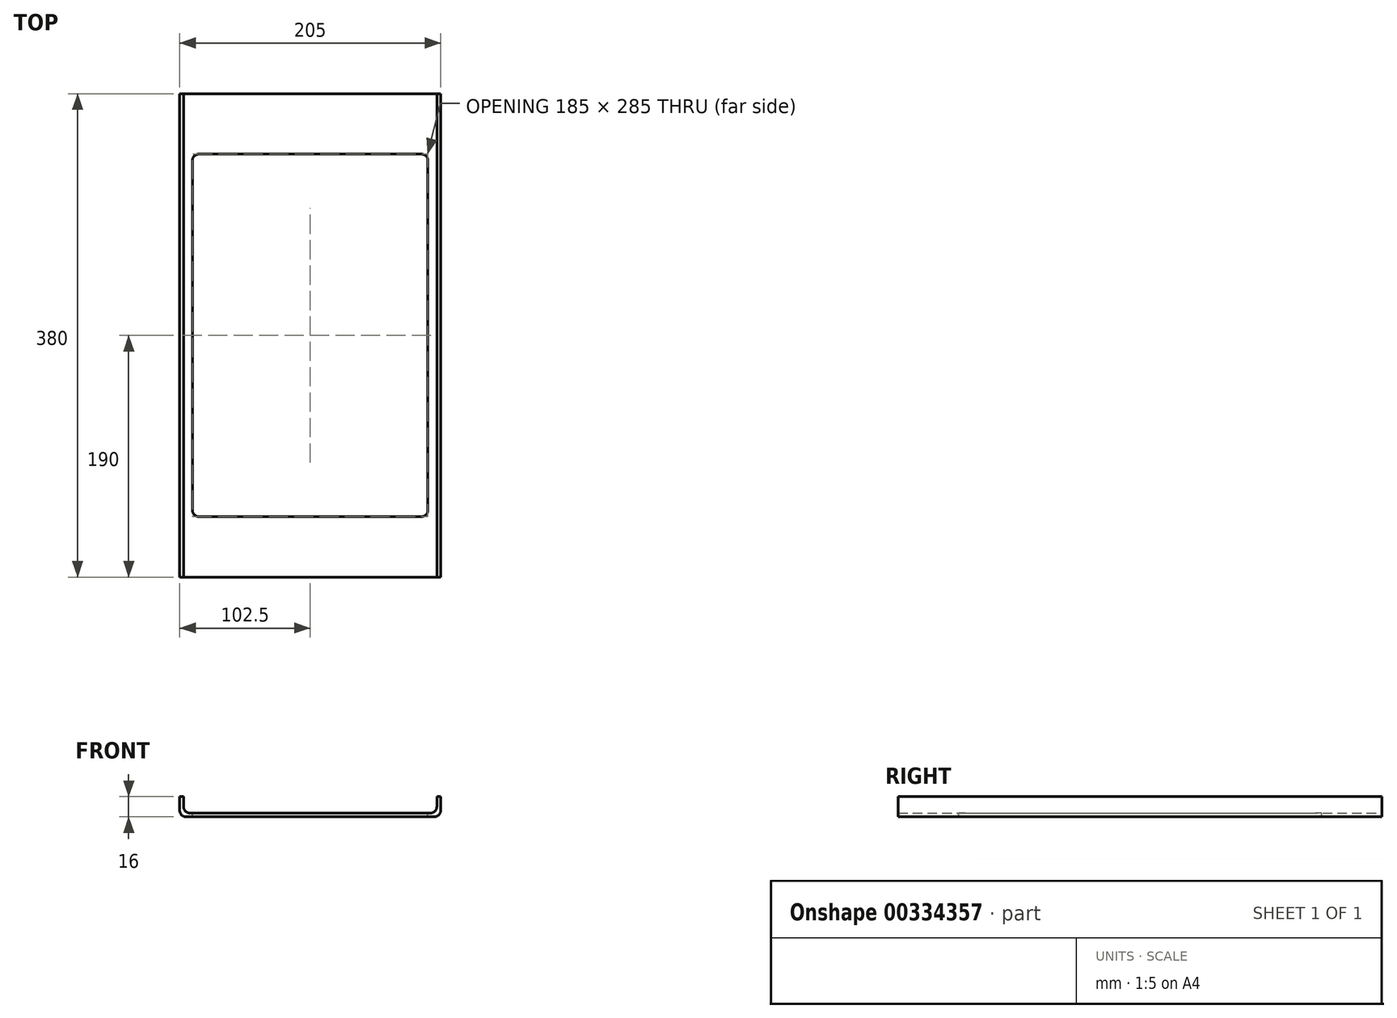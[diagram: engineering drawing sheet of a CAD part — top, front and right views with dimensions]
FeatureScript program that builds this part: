
annotation { "Feature Type Name" : "Feature", "Feature Type Description" : "" }
export const myFeature = defineFeature(function(context is Context, id is Id, definition is map)
    precondition{}
    {
        {
            var Q0;
            Q0=qCreatedBy(makeId("Front.planeOp"),FACE);
            var sketch = newSketch(context, id + "F0", { "sketchPlane" : qUnion([Q0])});
            skLineSegment(sketch, "E0.top", {"start": v(-102.5, -16) * mm, "end": v(102.5, -16) * mm});
            skLineSegment(sketch, "E0.left", {"start": v(-102.5, 0) * mm, "end": v(-102.5, -16) * mm});
            skLineSegment(sketch, "E0.right", {"start": v(102.5, 0) * mm, "end": v(102.5, -16) * mm});
            skPoint(sketch, "E0.middle", {"position": v(0, 0) * mm});
            skLineSegment(sketch, "E1.top", {"start": v(-99.5, -13) * mm, "end": v(99.5, -13) * mm});
            skLineSegment(sketch, "E1.left", {"start": v(-99.5, 0) * mm, "end": v(-99.5, -13) * mm});
            skLineSegment(sketch, "E1.right", {"start": v(99.5, 0) * mm, "end": v(99.5, -13) * mm});
            skLineSegment(sketch, "E2", {"start": v(102.5, 0) * mm, "end": v(99.5, 0) * mm});
            skPoint(sketch, "E0.bottom.end.orphan", {"position": v(102.5, 16) * mm});
            skPoint(sketch, "E1.bottom.end.orphan", {"position": v(99.5, 13) * mm});
            skLineSegment(sketch, "E3.trimOffspring", {"start": v(-99.5, 0) * mm, "end": v(-102.5, 0) * mm});
            skPoint(sketch, "E4.orphan", {"position": v(-102.5, 16) * mm});
            skPoint(sketch, "E5.orphan", {"position": v(-99.5, 13) * mm});
            skSolve(sketch);
        }
        {
            var Q0;
            Q0=qSketchRegion(id+"F0",true);
            extrude(context, id + "F1", {"entities" : qUnion([Q0]), "depth" : 380 * mm});
        }
        {
            var Q0;
            Q0=makeQuery(id+"F1.opExtrude","SWEPT_FACE",FACE,{"disambiguationData":[OSD([sQuery(id+"F0.wireOp",EDGE,"E1.top")])]});
            var sketch = newSketch(context, id + "F2", { "sketchPlane" : qUnion([Q0])});
            skLineSegment(sketch, "E6.bottom", {"start": v(-92.5, -332.5) * mm, "end": v(92.5, -332.5) * mm});
            skLineSegment(sketch, "E6.top", {"start": v(-92.5, -47.5) * mm, "end": v(92.5, -47.5) * mm});
            skLineSegment(sketch, "E6.left", {"start": v(-92.5, -332.5) * mm, "end": v(-92.5, -47.5) * mm});
            skLineSegment(sketch, "E6.right", {"start": v(92.5, -332.5) * mm, "end": v(92.5, -47.5) * mm});
            skPoint(sketch, "E6.middle", {"position": v(0, -190) * mm});
            skSolve(sketch);
        }
        {
            var Q0;
            Q0=makeQuery(id+"F2.imprint","IMPRINT",FACE,{"disambiguationData":[TD([[makeQuery(id+"F2.imprint","IMPRINT",EDGE,{"derivedFrom":sQuery(id+"F2.wireOp",EDGE,"E6.bottom")}),1.0]])]});
            extrude(context, id + "F3", {"entities" : qUnion([Q0]), "operationType" : NewBodyOperationType.REMOVE, "oppositeDirection" : true, "depth" : 3 * mm});
        }
        {
            var Q0;
            Q0=makeQuery(id+"F3.boolean.opBoolean","COPY",EDGE,{"derivedFrom":makeQuery(id+"F3.opExtrude","SWEPT_EDGE",EDGE,{"disambiguationData":[OSD([sQuery(id+"F2.wireOp",EDGE,"E6.top"),sQuery(id+"F2.wireOp",EDGE,"E6.left")])]})});
            var Q1;
            Q1=makeQuery(id+"F3.boolean.opBoolean","COPY",EDGE,{"derivedFrom":makeQuery(id+"F3.opExtrude","SWEPT_EDGE",EDGE,{"disambiguationData":[OSD([sQuery(id+"F2.wireOp",EDGE,"E6.top"),sQuery(id+"F2.wireOp",EDGE,"E6.right")])]})});
            var Q2;
            Q2=makeQuery(id+"F3.boolean.opBoolean","COPY",EDGE,{"derivedFrom":makeQuery(id+"F3.opExtrude","SWEPT_EDGE",EDGE,{"disambiguationData":[OSD([sQuery(id+"F2.wireOp",EDGE,"E6.bottom"),sQuery(id+"F2.wireOp",EDGE,"E6.left")])]})});
            var Q3;
            Q3=makeQuery(id+"F3.boolean.opBoolean","COPY",EDGE,{"derivedFrom":makeQuery(id+"F3.opExtrude","SWEPT_EDGE",EDGE,{"disambiguationData":[OSD([sQuery(id+"F2.wireOp",EDGE,"E6.bottom"),sQuery(id+"F2.wireOp",EDGE,"E6.right")])]})});
            fillet(context, id + "F4", {"entities" : qUnion([Q0, Q1, Q2, Q3]), "radius" : 5 * mm, "tangentPropagation" : true, "allowEdgeOverflow" : false});
        }
        {
            var Q0;
            Q0=makeQuery(id+"F1.opExtrude","SWEPT_EDGE",EDGE,{"disambiguationData":[OSD([sQuery(id+"F0.wireOp",EDGE,"E0.top"),sQuery(id+"F0.wireOp",EDGE,"E0.right")])]});
            var Q1;
            Q1=makeQuery(id+"F1.opExtrude","SWEPT_EDGE",EDGE,{"disambiguationData":[OSD([sQuery(id+"F0.wireOp",EDGE,"E0.top"),sQuery(id+"F0.wireOp",EDGE,"E0.left")])]});
            fillet(context, id + "F5", {"entities" : qUnion([Q0, Q1]), "radius" : 5 * mm, "tangentPropagation" : true, "allowEdgeOverflow" : false});
        }
        {
            var Q0;
            Q0=makeQuery(id+"F1.opExtrude","SWEPT_EDGE",EDGE,{"disambiguationData":[OSD([sQuery(id+"F0.wireOp",EDGE,"E1.top"),sQuery(id+"F0.wireOp",EDGE,"E1.left")])]});
            var Q1;
            Q1=makeQuery(id+"F1.opExtrude","SWEPT_EDGE",EDGE,{"disambiguationData":[OSD([sQuery(id+"F0.wireOp",EDGE,"E1.top"),sQuery(id+"F0.wireOp",EDGE,"E1.right")])]});
            fillet(context, id + "F6", {"entities" : qUnion([Q0, Q1]), "radius" : 5 * mm, "tangentPropagation" : true, "allowEdgeOverflow" : false});
        }
    });
